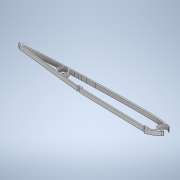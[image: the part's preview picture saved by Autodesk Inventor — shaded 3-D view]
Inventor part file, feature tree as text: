
AUTODESK INVENTOR PART (.ipt)
format: ipt  version: 2022 (Build 260153000, 153)  size: 296,960 bytes
history: native  units: mm
features: extrude x1, sketch x1
ambient origin geometry x8: Origin, YZ Plane, XZ Plane, XY Plane, X Axis, Y Axis, Z Axis, Center Point
bodies: Body1 (feature_tree)
feature tree (2):
  extrude  "Extrusion5"  Depth=368.759386mm
  sketch  "Sketch1"  dims[d31=34.456mm d50=368.759386mm d57=16.0mm d69=8.0mm d80=19.0mm d81=16.0mm d82=1.0mm d83=1.0mm d84=1.0mm d85=1.0mm d86=1.0mm d87=0.8mm d88=1.0mm d90=19.0mm d94=5.0mm d95=5.0mm d105=5.0mm d106=5.0mm d108=2.0mm d114=5.0mm d115=5.0mm d116=24.0mm d117=2.5mm d118=2.5mm d123=2.5mm d124=2.5mm d125=10.0mm d126=24.0mm d127=24.0mm d128=27.0mm d131=10.0mm d132=0.0mm d133=0.5mm d134=0.872665mm]
